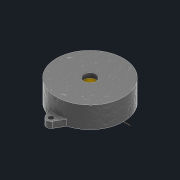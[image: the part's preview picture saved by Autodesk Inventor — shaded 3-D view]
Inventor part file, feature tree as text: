
AUTODESK INVENTOR PART (.ipt)
format: ipt  version: 2022 (Build 260153000, 153)  size: 117,760 bytes
history: native  units: mm
features: extrude x3, sketch x2, hole x1
ambient origin geometry x8: Origin, YZ Plane, XZ Plane, XY Plane, X Axis, Y Axis, Z Axis, Center Point
bodies: Solid1 (feature_tree)
feature tree (6):
  sketch  "Sketch1"  dims[d0=44.0mm d1=60.0deg]
  extrude  "Extrusion1"  TaperAngle=60.0deg  [1 undecoded]
  extrude  "Extrusion2"  Depth=3.0mm
  hole  "Hole1"  [1 undecoded]
  extrude  "Extrusion3"  Depth=4.0mm TaperAngle=0.0deg
  sketch  "Sketch2"  dims[d2=6.0mm d3=51.0mm d4=14.0mm d5=0.0mm d6=4.0mm d7=0.0mm d8=3.4mm d9=6.0mm d10=6.5mm d11=3.4mm d12=90.0deg d13=8.0mm d14=20.594885mm d15=8.0mm d16=3.0mm d17=0.0mm]
note: 2 required parameter values undecoded (feature->parameter linkage not recoverable at this tier; creation-order binding heuristic only, values carry confidence <= 0.55)
